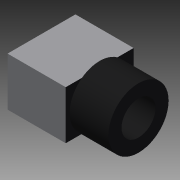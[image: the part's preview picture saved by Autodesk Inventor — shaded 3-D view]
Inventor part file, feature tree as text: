
AUTODESK INVENTOR PART (.ipt)
format: ipt  version: 2013 SP2 (Build 170200200, 200)  size: 117,760 bytes
history: native  units: mm
features: extrude x4, sketch x4, plane x1
ambient origin geometry x8: Origin, YZ Plane, XZ Plane, XY Plane, X Axis, Y Axis, Z Axis, Center Point
bodies: Solid1 (feature_tree)
feature tree (9):
  plane  "Work Plane1"
  extrude  "Extrusion1"  Depth=7.0mm
  extrude  "Extrusion2"  Depth=6.2mm
  extrude  "Extrusion3"  Depth=3.5mm
  extrude  "Extrusion4"  Depth=3.0mm
  sketch  "Sketch1"  dims[d0=6.0mm d2=7.0mm]
  sketch  "Sketch2"  dims[d3=5.0mm d4=0.0mm d5=6.2mm]
  sketch  "Sketch3"  dims[d7=4.0mm d8=0.0mm d9=3.5mm]
  sketch  "Sketch4"  dims[d11=7.0mm d12=0.0mm d13=3.0mm d15=6.0mm d16=0.0mm]
